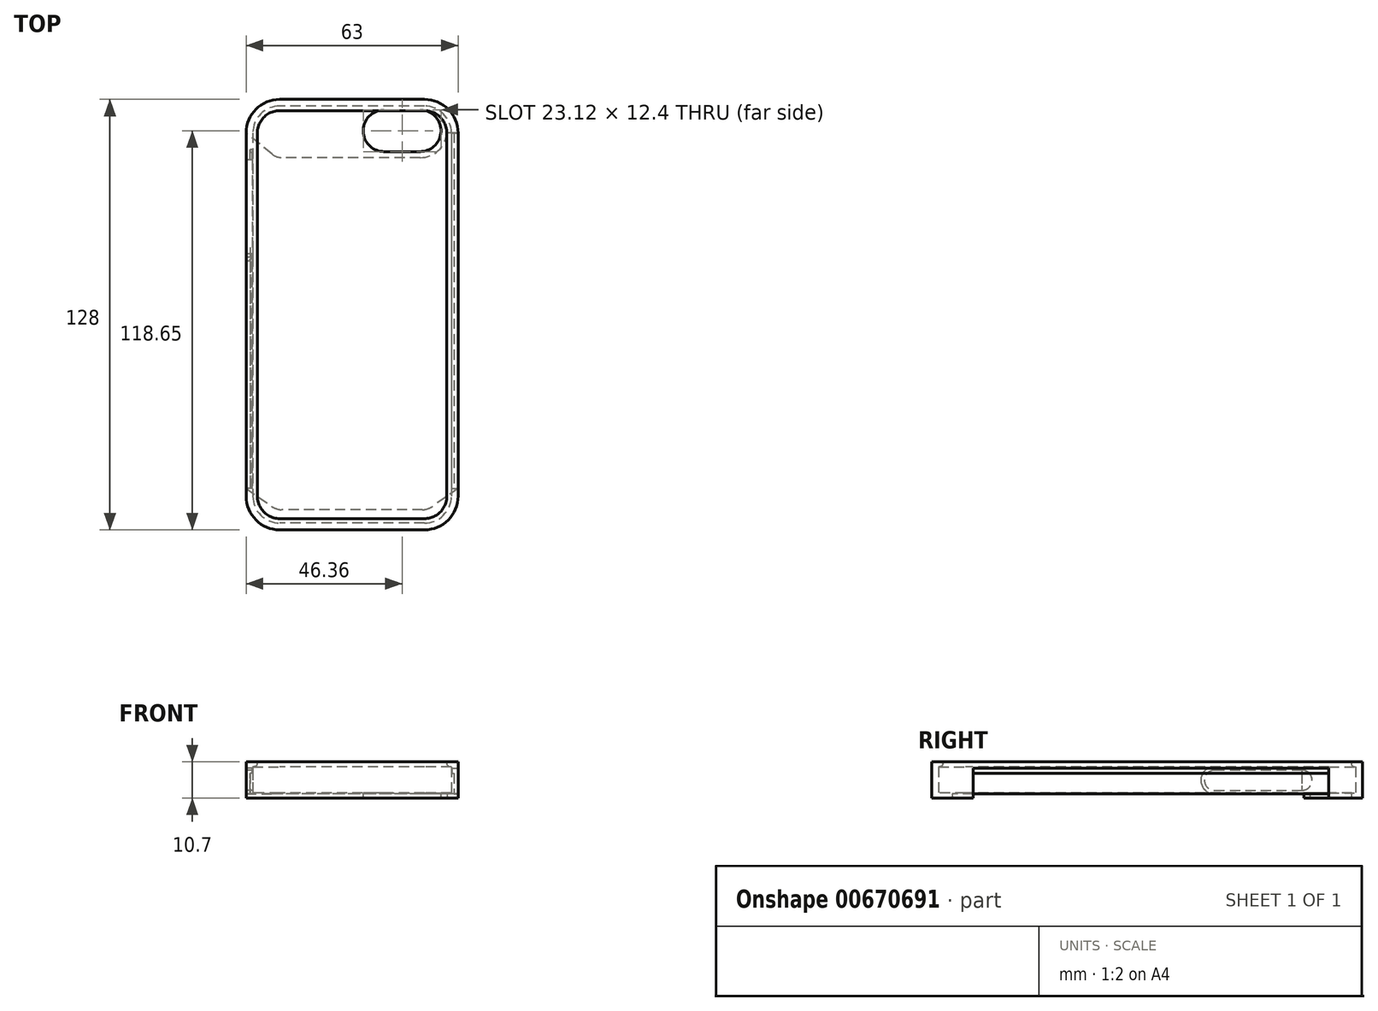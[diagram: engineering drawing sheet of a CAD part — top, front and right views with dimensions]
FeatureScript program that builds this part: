
annotation { "Feature Type Name" : "Feature", "Feature Type Description" : "" }
export const myFeature = defineFeature(function(context is Context, id is Id, definition is map)
    precondition{}
    {
        {
            var Q0;
            Q0=qCreatedBy(makeId("Top.planeOp"),FACE);
            var sketch = newSketch(context, id + "F0", { "sketchPlane" : qUnion([Q0])});
            skLineSegment(sketch, "E0.bottom", {"start": v(21.5, 62) * mm, "end": v(-21.5, 62) * mm});
            skLineSegment(sketch, "E0.top", {"start": v(21.5, -62) * mm, "end": v(-21.5, -62) * mm});
            skLineSegment(sketch, "E0.left", {"start": v(29.5, 54) * mm, "end": v(29.5, -54) * mm});
            skLineSegment(sketch, "E0.right", {"start": v(-29.5, 54) * mm, "end": v(-29.5, -54) * mm});
            skPoint(sketch, "E0.middle", {"position": v(0, 0) * mm});
            skPoint(sketch, "E1.visualSharp", {"position": v(-29.5, 62) * mm});
            skArc(sketch, "E1.filletArc", {"start": v(-21.5, 62) * mm, "mid": v(-27.16, 59.66) * mm, "end": v(-29.5, 54) * mm});
            skPoint(sketch, "E2.visualSharp", {"position": v(29.5, 62) * mm});
            skArc(sketch, "E2.filletArc", {"start": v(29.5, 54) * mm, "mid": v(27.16, 59.66) * mm, "end": v(21.5, 62) * mm});
            skPoint(sketch, "E3.visualSharp", {"position": v(29.5, -62) * mm});
            skArc(sketch, "E3.filletArc", {"start": v(21.5, -62) * mm, "mid": v(27.16, -59.66) * mm, "end": v(29.5, -54) * mm});
            skPoint(sketch, "E4.visualSharp", {"position": v(-29.5, -62) * mm});
            skArc(sketch, "E4.filletArc", {"start": v(-29.5, -54) * mm, "mid": v(-27.16, -59.66) * mm, "end": v(-21.5, -62) * mm});
            skArc(sketch, "E5.0", {"start": v(31.5, 54) * mm, "mid": v(28.57, 61.07) * mm, "end": v(21.5, 64) * mm});
            skLineSegment(sketch, "E5.1", {"start": v(31.5, 54) * mm, "end": v(31.5, -54) * mm});
            skLineSegment(sketch, "E5.2", {"start": v(21.5, 64) * mm, "end": v(-21.5, 64) * mm});
            skArc(sketch, "E5.3", {"start": v(21.5, -64) * mm, "mid": v(28.57, -61.07) * mm, "end": v(31.5, -54) * mm});
            skArc(sketch, "E5.4", {"start": v(-21.5, 64) * mm, "mid": v(-28.57, 61.07) * mm, "end": v(-31.5, 54) * mm});
            skLineSegment(sketch, "E5.5", {"start": v(-31.5, 54) * mm, "end": v(-31.5, -54) * mm});
            skArc(sketch, "E5.6", {"start": v(-31.5, -54) * mm, "mid": v(-28.57, -61.07) * mm, "end": v(-21.5, -64) * mm});
            skLineSegment(sketch, "E5.7", {"start": v(21.5, -64) * mm, "end": v(-21.5, -64) * mm});
            skLineSegment(sketch, "E6", {"start": v(0, 62) * mm, "end": v(0, 64) * mm, "construction": true});
            skLineSegment(sketch, "E7", {"start": v(0, -64) * mm, "end": v(0, -62) * mm, "construction": true});
            skSolve(sketch);
        }
        {
            var Q0;
            Q0=qSketchRegion(id+"F0",true);
            extrude(context, id + "F1", {"entities" : qUnion([Q0]), "depth" : 9.2 * mm, "offsetDistance" : 25 * mm});
        }
        {
            var Q0;
            Q0=makeQuery(id+"F0.imprint","IMPRINT",FACE,{"disambiguationData":[TD([[makeQuery(id+"F0.imprint","IMPRINT",EDGE,{"derivedFrom":sQuery(id+"F0.wireOp",EDGE,"E0.bottom")}),1.0]])]});
            extrude(context, id + "F2", {"entities" : qUnion([Q0]), "operationType" : NewBodyOperationType.ADD, "depth" : 1.5 * mm, "offsetDistance" : 25 * mm});
        }
        {
            var Q0;
            Q0=makeQuery(id+"F1.opExtrude","SWEPT_FACE",FACE,{"disambiguationData":[OSD([sQuery(id+"F0.wireOp",EDGE,"E5.5")])]});
            var sketch = newSketch(context, id + "F3", { "sketchPlane" : qUnion([Q0])});
            skLineSegment(sketch, "E8", {"start": v(0, 9.2) * mm, "end": v(0, 0) * mm, "construction": true});
            skLineSegment(sketch, "E9", {"start": v(-17, 9.2) * mm, "end": v(-17, 0) * mm, "construction": true});
            skLineSegment(sketch, "E10", {"start": v(-49, 9.2) * mm, "end": v(-49, 0) * mm, "construction": true});
            skPoint(sketch, "E11", {"position": v(-49, 5.25) * mm});
            skPoint(sketch, "E12", {"position": v(-17, 5.25) * mm});
            skPoint(sketch, "E13", {"position": v(-46, 5.25) * mm});
            skPoint(sketch, "E14", {"position": v(-20, 5.25) * mm});
            skArc(sketch, "E15", {"start": v(-46, 2.25) * mm, "mid": v(-49, 5.25) * mm, "end": v(-46, 8.25) * mm});
            skArc(sketch, "E16", {"start": v(-20, 8.25) * mm, "mid": v(-17, 5.25) * mm, "end": v(-20, 2.25) * mm});
            skLineSegment(sketch, "E17", {"start": v(-46, 8.25) * mm, "end": v(-20, 8.25) * mm});
            skLineSegment(sketch, "E18", {"start": v(-20, 2.25) * mm, "end": v(-46, 2.25) * mm});
            skSolve(sketch);
        }
        {
            var Q0;
            Q0=qSketchRegion(id+"F3",true);
            extrude(context, id + "F4", {"entities" : qUnion([Q0]), "operationType" : NewBodyOperationType.REMOVE, "oppositeDirection" : true, "depth" : 10 * mm, "offsetDistance" : 25 * mm});
        }
        {
            var Q0;
            Q0=qSketchRegion(id+"F3",true);
            extrude(context, id + "F5", {"entities" : qUnion([Q0]), "operationType" : NewBodyOperationType.REMOVE, "oppositeDirection" : true, "depth" : 10 * mm, "offsetDistance" : 25 * mm});
        }
        {
            var Q0;
            Q0=makeQuery(id+"F0ujZ4bz4C0mLiR_1.boolean.opBoolean","MERGE",FACE,{"derivedFrom":[makeQuery(id+"FQ2Wo6Bxvnj0YfB_1.boolean.opBoolean","MERGE",FACE,{"derivedFrom":[makeQuery(id+"F2.opExtrude","CAP_FACE",FACE,{"disambiguationData":[OSD([sQuery(id+"F0.wireOp",EDGE,"E0.bottom"),sQuery(id+"F0.wireOp",EDGE,"E0.top"),sQuery(id+"F0.wireOp",EDGE,"E0.left"),sQuery(id+"F0.wireOp",EDGE,"E0.right"),sQuery(id+"F0.wireOp",EDGE,"E1.filletArc"),sQuery(id+"F0.wireOp",EDGE,"E2.filletArc"),sQuery(id+"F0.wireOp",EDGE,"E3.filletArc"),sQuery(id+"F0.wireOp",EDGE,"E4.filletArc")])],"isStart":false}),makeQuery(id+"FQ2Wo6Bxvnj0YfB_1.opExtrude","SWEPT_FACE",FACE,{"disambiguationData":[OSD([sQuery(id+"FqBCXfSKVOIVOjJ_1.wireOp",EDGE,"6ESOPYnS-w2do-941M-JKbI-ah7n0wvXEvAS")])]})]}),makeQuery(id+"F0ujZ4bz4C0mLiR_1.opExtrude","SWEPT_FACE",FACE,{"disambiguationData":[OSD([sQuery(id+"FVHNuu85IpXXWSm_1.wireOp",EDGE,"teC8dt7o-NYte-iiF7-KThB-fhYtOqZq8K3d")])]})]});
            var sketch = newSketch(context, id + "F6", { "sketchPlane" : qUnion([Q0])});
            skPoint(sketch, "E19", {"position": v(20.22, 54.65) * mm});
            skArc(sketch, "E20", {"start": v(20.22, 48.45) * mm, "mid": v(26.42, 54.65) * mm, "end": v(20.22, 60.85) * mm});
            skPoint(sketch, "E21", {"position": v(9.5, 54.65) * mm});
            skArc(sketch, "E22", {"start": v(9.5, 60.85) * mm, "mid": v(3.3, 54.65) * mm, "end": v(9.5, 48.45) * mm});
            skLineSegment(sketch, "E23", {"start": v(9.5, 60.85) * mm, "end": v(20.22, 60.85) * mm});
            skLineSegment(sketch, "E24", {"start": v(20.22, 48.45) * mm, "end": v(9.5, 48.45) * mm});
            skSolve(sketch);
        }
        {
            var Q0;
            Q0=qSketchRegion(id+"F6",true);
            extrude(context, id + "F7", {"entities" : qUnion([Q0]), "operationType" : NewBodyOperationType.REMOVE, "oppositeDirection" : true, "depth" : 25 * mm, "offsetDistance" : 25 * mm});
        }
        {
            var Q0;
            Q0=makeQuery(id+"F1.opExtrude","CAP_FACE",FACE,{"disambiguationData":[OSD([sQuery(id+"F0.wireOp",EDGE,"E0.bottom"),sQuery(id+"F0.wireOp",EDGE,"E0.top"),sQuery(id+"F0.wireOp",EDGE,"E0.left"),sQuery(id+"F0.wireOp",EDGE,"E0.right"),sQuery(id+"F0.wireOp",EDGE,"E1.filletArc"),sQuery(id+"F0.wireOp",EDGE,"E2.filletArc"),sQuery(id+"F0.wireOp",EDGE,"E3.filletArc"),sQuery(id+"F0.wireOp",EDGE,"E4.filletArc"),sQuery(id+"F0.wireOp",EDGE,"E5.0"),sQuery(id+"F0.wireOp",EDGE,"E5.1"),sQuery(id+"F0.wireOp",EDGE,"E5.2"),sQuery(id+"F0.wireOp",EDGE,"E5.3"),sQuery(id+"F0.wireOp",EDGE,"E5.4"),sQuery(id+"F0.wireOp",EDGE,"E5.5"),sQuery(id+"F0.wireOp",EDGE,"E5.6"),sQuery(id+"F0.wireOp",EDGE,"E5.7")])],"isStart":false});
            var sketch = newSketch(context, id + "F8", { "sketchPlane" : qUnion([Q0])});
            skLineSegment(sketch, "E25", {"start": v(0, 64) * mm, "end": v(0, 62) * mm});
            skLineSegment(sketch, "E26", {"start": v(0, 64) * mm, "end": v(0.16, 64) * mm});
            skLineSegment(sketch, "E27", {"start": v(0.16, 64) * mm, "end": v(0.16, 62) * mm});
            skLineSegment(sketch, "E28", {"start": v(0.16, 62) * mm, "end": v(0, 62) * mm});
            skSolve(sketch);
        }
        {
            var Q0;
            Q0 = qSketchRegion(id + "F8", true);
            extrude(context, id + "F9", {"entities" : qUnion([Q0]), "operationType" : NewBodyOperationType.ADD, "depth" : 1.5 * mm, "offsetDistance" : 25 * mm});
        }
        {
            var Q0;
            Q0=makeQuery(id+"F9.opExtrude","SWEPT_FACE",FACE,{"disambiguationData":[OSD([sQuery(id+"F8.wireOp",EDGE,"E25")])]});
            var sketch = newSketch(context, id + "F10", { "sketchPlane" : qUnion([Q0])});
            skLineSegment(sketch, "E29", {"start": v(-62, 10.7) * mm, "end": v(-61.25, 10.7) * mm});
            skLineSegment(sketch, "E30", {"start": v(-61.05, 9.53) * mm, "end": v(-62, 9.2) * mm});
            skPoint(sketch, "E31.visualSharp", {"position": v(-57.74, 10.7) * mm});
            skArc(sketch, "E31.filletArc", {"start": v(-61.05, 9.53) * mm, "mid": v(-60.66, 10.2) * mm, "end": v(-61.25, 10.7) * mm});
            skSolve(sketch);
        }
        {
            var Q0;
            {var subQ0=sQuery(id+"F8.wireOp",EDGE,"E25");Q0=makeQuery(id+"F10.imprint","IMPRINT",FACE,{"disambiguationData":[TD([[makeQuery(id+"F10.imprint","IMPRINT",EDGE,{"derivedFrom":makeQuery(id+"F9.opExtrude","CAP_EDGE",EDGE,{"disambiguationData":[OSD([subQ0])],"isStart":false})}),-1.0]])]});}
            var Q1;
            Q1=makeQuery(id+"F10.imprint","IMPRINT",FACE,{"disambiguationData":[TD([[makeQuery(id+"F10.imprint","IMPRINT",EDGE,{"derivedFrom":sQuery(id+"F10.wireOp",EDGE,"E29")}),-1.0]])]});
            var Q2;
            {var subQ0=sQuery(id+"F0.wireOp",EDGE,"E1.filletArc");var subQ1=sQuery(id+"F0.wireOp",EDGE,"E0.bottom");Q2=makeQuery(id+"F9.boolean.opBoolean","SPLIT",EDGE,{"disambiguationData":[TD([makeQuery(id+"F1.opExtrude","SWEPT_FACE",FACE,{"disambiguationData":[OSD([subQ0])]})])],"derivedFrom":makeQuery(id+"F1.opExtrude","CAP_EDGE",EDGE,{"disambiguationData":[OSD([subQ1])],"isStart":false})});}
            var Q3;
            Q3=makeQuery(id+"F1.opExtrude","CAP_EDGE",EDGE,{"disambiguationData":[OSD([sQuery(id+"F0.wireOp",EDGE,"E1.filletArc")])],"isStart":false});
            var Q4;
            Q4=makeQuery(id+"F1.opExtrude","CAP_EDGE",EDGE,{"disambiguationData":[OSD([sQuery(id+"F0.wireOp",EDGE,"E0.right")])],"isStart":false});
            var Q5;
            {var subQ0=sQuery(id+"F0.wireOp",EDGE,"E2.filletArc");var subQ1=sQuery(id+"F0.wireOp",EDGE,"E0.bottom");Q5=makeQuery(id+"F9.boolean.opBoolean","SPLIT",EDGE,{"disambiguationData":[TD([makeQuery(id+"F1.opExtrude","SWEPT_FACE",FACE,{"disambiguationData":[OSD([subQ0])]})])],"derivedFrom":makeQuery(id+"F1.opExtrude","CAP_EDGE",EDGE,{"disambiguationData":[OSD([subQ1])],"isStart":false})});}
            var Q6;
            Q6=makeQuery(id+"F1.opExtrude","CAP_EDGE",EDGE,{"disambiguationData":[OSD([sQuery(id+"F0.wireOp",EDGE,"E2.filletArc")])],"isStart":false});
            var Q7;
            Q7=makeQuery(id+"F1.opExtrude","CAP_EDGE",EDGE,{"disambiguationData":[OSD([sQuery(id+"F0.wireOp",EDGE,"E0.left")])],"isStart":false});
            var Q8;
            Q8=makeQuery(id+"F1.opExtrude","CAP_EDGE",EDGE,{"disambiguationData":[OSD([sQuery(id+"F0.wireOp",EDGE,"E4.filletArc")])],"isStart":false});
            var Q9;
            Q9=makeQuery(id+"F1.opExtrude","CAP_EDGE",EDGE,{"disambiguationData":[OSD([sQuery(id+"F0.wireOp",EDGE,"E0.top")])],"isStart":false});
            var Q10;
            Q10=makeQuery(id+"F1.opExtrude","CAP_EDGE",EDGE,{"disambiguationData":[OSD([sQuery(id+"F0.wireOp",EDGE,"E3.filletArc")])],"isStart":false});
            sweep(context, id + "F11", {"operationType" : NewBodyOperationType.ADD, "profiles" : qUnion([Q0, Q1]), "path" : qUnion([Q2, Q3, Q4, Q5, Q6, Q7, Q8, Q9, Q10])});
        }
        {
            var Q0;
            Q0=makeQuery(id+"F11.opSweep","CAP_FACE",FACE,{"disambiguationData":[OSD([sQuery(id+"F0.wireOp",EDGE,"E0.bottom"),sQuery(id+"F0.wireOp",EDGE,"E5.2"),sQuery(id+"F8.wireOp",EDGE,"E25"),sQuery(id+"F8.wireOp",EDGE,"E26"),sQuery(id+"F8.wireOp",EDGE,"E28"),sQuery(id+"F10.wireOp",EDGE,"E29"),sQuery(id+"F10.wireOp",EDGE,"E30"),sQuery(id+"F10.wireOp",EDGE,"E31.filletArc")])],"isStart":true});
            extrude(context, id + "F12", {"entities" : qUnion([Q0]), "operationType" : NewBodyOperationType.ADD, "depth" : .2 * mm, "offsetDistance" : 25 * mm});
        }
        {
            var Q0;
            {var subQ0=sQuery(id+"F0.wireOp",EDGE,"E4.filletArc");var subQ1=sQuery(id+"F0.wireOp",EDGE,"E3.filletArc");var subQ2=sQuery(id+"F0.wireOp",EDGE,"E2.filletArc");var subQ3=sQuery(id+"F0.wireOp",EDGE,"E1.filletArc");var subQ4=sQuery(id+"F0.wireOp",EDGE,"E0.right");var subQ5=sQuery(id+"F0.wireOp",EDGE,"E0.left");var subQ6=sQuery(id+"F0.wireOp",EDGE,"E0.top");var subQ7=sQuery(id+"F0.wireOp",EDGE,"E0.bottom");Q0=makeQuery(id+"F2.boolean.opBoolean","MERGE",FACE,{"derivedFrom":[makeQuery(id+"F1.opExtrude","CAP_FACE",FACE,{"disambiguationData":[OSD([subQ7,subQ6,subQ5,subQ4,subQ3,subQ2,subQ1,subQ0,sQuery(id+"F0.wireOp",EDGE,"E5.0"),sQuery(id+"F0.wireOp",EDGE,"E5.1"),sQuery(id+"F0.wireOp",EDGE,"E5.2"),sQuery(id+"F0.wireOp",EDGE,"E5.3"),sQuery(id+"F0.wireOp",EDGE,"E5.4"),sQuery(id+"F0.wireOp",EDGE,"E5.5"),sQuery(id+"F0.wireOp",EDGE,"E5.6"),sQuery(id+"F0.wireOp",EDGE,"E5.7")])],"isStart":true}),makeQuery(id+"F2.opExtrude","CAP_FACE",FACE,{"disambiguationData":[OSD([subQ7,subQ6,subQ5,subQ4,subQ3,subQ2,subQ1,subQ0])],"isStart":true})]});}
            var sketch = newSketch(context, id + "F13", { "sketchPlane" : qUnion([Q0])});
            skLineSegment(sketch, "E32", {"start": v(-31.5, 51.7) * mm, "end": v(-23.8, 57.1) * mm});
            skLineSegment(sketch, "E33", {"start": v(-20.92, 58) * mm, "end": v(0, 58) * mm});
            skLineSegment(sketch, "E34.MirrorCS", {"start": v(20.92, 58) * mm, "end": v(0, 58) * mm});
            skLineSegment(sketch, "E35.MirrorCS", {"start": v(31.5, 51.7) * mm, "end": v(23.8, 57.1) * mm});
            skCircle(sketch, "E36", {"center": v(20.22, -54.65) * mm, "radius": 8 * mm, "construction": true});
            skLineSegment(sketch, "E37", {"start": v(31.5, -54) * mm, "end": v(28.2, -54) * mm});
            skLineSegment(sketch, "E38", {"start": v(20.22, -46.65) * mm, "end": v(-20.72, -46.65) * mm});
            skLineSegment(sketch, "E39", {"start": v(-23.88, -47.78) * mm, "end": v(-31.5, -54) * mm});
            skArc(sketch, "E40", {"start": v(28.2, -54) * mm, "mid": v(25.64, -48.77) * mm, "end": v(20.22, -46.65) * mm});
            skPoint(sketch, "E41.visualSharp", {"position": v(-22.5, -46.65) * mm});
            skArc(sketch, "E41.filletArc", {"start": v(-20.72, -46.65) * mm, "mid": v(-22.4, -46.94) * mm, "end": v(-23.88, -47.78) * mm});
            skPoint(sketch, "E42.visualSharp", {"position": v(-22.5, 58) * mm});
            skArc(sketch, "E42.filletArc", {"start": v(-20.92, 58) * mm, "mid": v(-22.43, 57.77) * mm, "end": v(-23.8, 57.1) * mm});
            skPoint(sketch, "E43.visualSharp", {"position": v(22.5, 58) * mm});
            skArc(sketch, "E43.filletArc", {"start": v(23.8, 57.1) * mm, "mid": v(22.43, 57.77) * mm, "end": v(20.92, 58) * mm});
            skSolve(sketch);
        }
        {
            var Q0;
            {var subQ2=sQuery(id+"F13.wireOp",EDGE,"E32");Q0=makeQuery(id+"F13.imprint","IMPRINT",FACE,{"disambiguationData":[TD([[makeQuery(id+"F13.imprint","IMPRINT",EDGE,{"derivedFrom":subQ2}),-1.0]])]});}
            extrude(context, id + "F14", {"entities" : qUnion([Q0]), "operationType" : NewBodyOperationType.REMOVE, "oppositeDirection" : true, "depth" : 1.2 * mm, "offsetDistance" : 25 * mm});
        }
        {
            var Q0;
            Q0=makeQuery(id+"F11.boolean.opBoolean","MERGE",FACE,{"derivedFrom":[makeQuery(id+"F1.opExtrude","SWEPT_FACE",FACE,{"disambiguationData":[OSD([sQuery(id+"F0.wireOp",EDGE,"E5.1")])]}),makeQuery(id+"F11.opSweep","SWEPT_FACE",FACE,{"disambiguationData":[OSD([sQuery(id+"F0.wireOp",EDGE,"E0.left"),sQuery(id+"F0.wireOp",EDGE,"E5.2"),sQuery(id+"F8.wireOp",EDGE,"E25"),sQuery(id+"F8.wireOp",EDGE,"E26")])]})]});
            var sketch = newSketch(context, id + "F15", { "sketchPlane" : qUnion([Q0])});
            skLineSegment(sketch, "E44", {"start": v(-51.7, 1.2) * mm, "end": v(-51.7, 8.8) * mm});
            skLineSegment(sketch, "E45", {"start": v(-51.7, 8.8) * mm, "end": v(54, 8.8) * mm});
            skLineSegment(sketch, "E46", {"start": v(-51.7, 7.3) * mm, "end": v(54, 7.3) * mm});
            skSolve(sketch);
        }
        {
            var Q0;
            {var subQ3=sQuery(id+"F15.wireOp",EDGE,"E46");Q0=makeQuery(id+"F15.imprint","IMPRINT",FACE,{"disambiguationData":[TD([[makeQuery(id+"F15.imprint","IMPRINT",EDGE,{"derivedFrom":subQ3}),-1.0]])]});}
            extrude(context, id + "F16", {"entities" : qUnion([Q0]), "operationType" : NewBodyOperationType.REMOVE, "oppositeDirection" : true, "depth" : 1.2 * mm, "offsetDistance" : 25 * mm});
        }
        {
            var Q0;
            {var subQ0=sQuery(id+"F15.wireOp",EDGE,"E45");Q0=makeQuery(id+"F15.imprint","IMPRINT",FACE,{"disambiguationData":[TD([[makeQuery(id+"F15.imprint","IMPRINT",EDGE,{"derivedFrom":subQ0}),-1.0]])]});}
            extrude(context, id + "F17", {"entities" : qUnion([Q0]), "operationType" : NewBodyOperationType.REMOVE, "oppositeDirection" : true, "depth" : 1.8 * mm, "offsetDistance" : 25 * mm});
        }
        {
            var Q0;
            Q0=makeQuery(id+"F11.boolean.opBoolean","MERGE",FACE,{"derivedFrom":[makeQuery(id+"F1.opExtrude","SWEPT_FACE",FACE,{"disambiguationData":[OSD([sQuery(id+"F0.wireOp",EDGE,"E5.5")])]}),makeQuery(id+"F11.opSweep","SWEPT_FACE",FACE,{"disambiguationData":[OSD([sQuery(id+"F0.wireOp",EDGE,"E0.right"),sQuery(id+"F0.wireOp",EDGE,"E5.2"),sQuery(id+"F8.wireOp",EDGE,"E25"),sQuery(id+"F8.wireOp",EDGE,"E26")])]})]});
            var sketch = newSketch(context, id + "F18", { "sketchPlane" : qUnion([Q0])});
            skLineSegment(sketch, "E47", {"start": v(-54, 8.8) * mm, "end": v(51.7, 8.8) * mm, "construction": true});
            skLineSegment(sketch, "E48", {"start": v(51.7, 8.8) * mm, "end": v(51.7, 1.2) * mm});
            skLineSegment(sketch, "E49", {"start": v(-54, 7.3) * mm, "end": v(-49.5, 7.3) * mm});
            skLineSegment(sketch, "E50", {"start": v(-50, 8.8) * mm, "end": v(-54, 8.8) * mm});
            skArc(sketch, "E51", {"start": v(-46, 1.2) * mm, "mid": v(-49.92, 4.24) * mm, "end": v(-47.95, 8.8) * mm});
            skLineSegment(sketch, "E52", {"start": v(-54, 8.8) * mm, "end": v(-47.95, 8.8) * mm});
            skArc(sketch, "E53", {"start": v(-20, 1.2) * mm, "mid": v(-16.08, 4.24) * mm, "end": v(-18.05, 8.8) * mm});
            skLineSegment(sketch, "E54", {"start": v(-16.5, 7.3) * mm, "end": v(51.7, 7.3) * mm});
            skLineSegment(sketch, "E55", {"start": v(51.7, 8.8) * mm, "end": v(-18.05, 8.8) * mm});
            skSolve(sketch);
        }
        {
            var Q0;
            {var subQ0=sQuery(id+"F18.wireOp",EDGE,"E49");Q0=makeQuery(id+"F18.imprint","IMPRINT",FACE,{"disambiguationData":[TD([[makeQuery(id+"F18.imprint","IMPRINT",EDGE,{"derivedFrom":subQ0}),-1.0]])]});}
            var Q1;
            {var subQ4=sQuery(id+"F18.wireOp",EDGE,"E54");Q1=makeQuery(id+"F18.imprint","IMPRINT",FACE,{"disambiguationData":[TD([[makeQuery(id+"F18.imprint","IMPRINT",EDGE,{"derivedFrom":subQ4}),-1.0]])]});}
            extrude(context, id + "F19", {"entities" : qUnion([Q0, Q1]), "operationType" : NewBodyOperationType.REMOVE, "oppositeDirection" : true, "depth" : 1.2 * mm, "offsetDistance" : 25 * mm});
        }
        {
            var Q0;
            {var subQ2=sQuery(id+"F18.wireOp",EDGE,"E49");Q0=makeQuery(id+"F18.imprint","IMPRINT",FACE,{"disambiguationData":[TD([[makeQuery(id+"F18.imprint","IMPRINT",EDGE,{"derivedFrom":subQ2}),1.0]])]});}
            var Q1;
            {var subQ0=sQuery(id+"F18.wireOp",EDGE,"E54");Q1=makeQuery(id+"F18.imprint","IMPRINT",FACE,{"disambiguationData":[TD([[makeQuery(id+"F18.imprint","IMPRINT",EDGE,{"derivedFrom":subQ0}),1.0]])]});}
            extrude(context, id + "F20", {"entities" : qUnion([Q0, Q1]), "operationType" : NewBodyOperationType.REMOVE, "oppositeDirection" : true, "depth" : 1.8 * mm, "offsetDistance" : 25 * mm});
        }
        {
            var Q0;
            {var subQ0=sQuery(id+"F0.wireOp",EDGE,"E5.5");var subQ1=makeQuery(id+"F14.boolean.opBoolean","COPY",EDGE,{"derivedFrom":makeQuery(id+"F14.opExtrude","CAP_EDGE",EDGE,{"disambiguationData":[OSD([subQ0])],"isStart":false})});Q0=makeQuery(id+"F19.boolean.opBoolean","COPY",FACE,{"derivedFrom":makeQuery(id+"F19.opExtrude","SWEPT_FACE",FACE,{"disambiguationData":[OSD([subQ0]),TDD([makeQuery(id+"F18.imprint","IMPRINT",EDGE,{"disambiguationData":[TD([[makeQuery(id+"F18.imprint","INTERSECT",VERTEX,{"derivedFrom":[subQ1,sQuery(id+"F18.wireOp",EDGE,"E51")]}),1.0]])],"derivedFrom":subQ1})])]})});}
            extrude(context, id + "F21", {"entities" : qUnion([Q0]), "operationType" : NewBodyOperationType.ADD, "depth" : 8 * mm, "offsetDistance" : 25 * mm});
        }
    });
